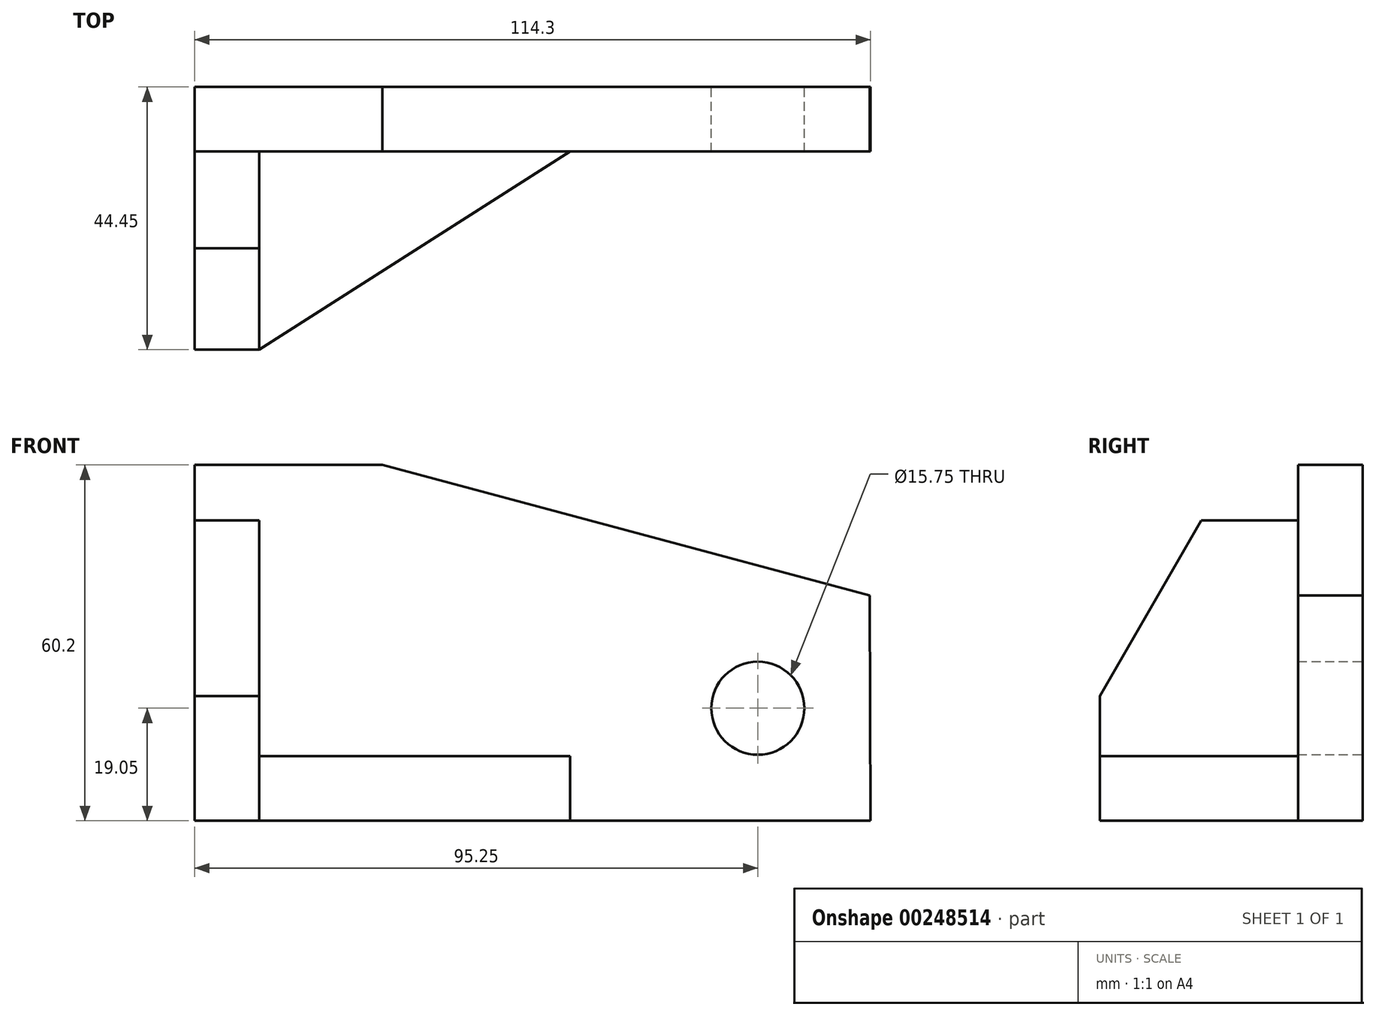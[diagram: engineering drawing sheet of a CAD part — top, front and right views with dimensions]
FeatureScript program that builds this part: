
annotation { "Feature Type Name" : "Feature", "Feature Type Description" : "" }
export const myFeature = defineFeature(function(context is Context, id is Id, definition is map)
    precondition{}
    {
        {
            var Q0;
            Q0=qCreatedBy(makeId("Top.planeOp"),FACE);
            var sketch = newSketch(context, id + "F0", { "sketchPlane" : qUnion([Q0])});
            skLineSegment(sketch, "E0", {"start": v(10.92, -10.92) * mm, "end": v(10.92, -44.45) * mm});
            skLineSegment(sketch, "E1", {"start": v(10.92, -10.92) * mm, "end": v(63.5, -10.92) * mm});
            skLineSegment(sketch, "E2", {"start": v(63.5, -10.92) * mm, "end": v(10.92, -44.45) * mm});
            skSolve(sketch);
        }
        {
            var Q0;
            Q0=qCreatedBy(makeId("Right.planeOp"),FACE);
            var sketch = newSketch(context, id + "F1", { "sketchPlane" : qUnion([Q0])});
            skLineSegment(sketch, "E3", {"start": v(0, 0) * mm, "end": v(-44.45, 0) * mm});
            skLineSegment(sketch, "E4", {"start": v(-44.45, 0) * mm, "end": v(-44.45, 21.08) * mm});
            skLineSegment(sketch, "E5", {"start": v(-44.45, 21.08) * mm, "end": v(-44.45, 50.8) * mm, "construction": true});
            skPoint(sketch, "E6", {"position": v(-10.92, 0) * mm});
            skPoint(sketch, "E7", {"position": v(0, 0) * mm});
            skLineSegment(sketch, "E8", {"start": v(-44.45, 50.8) * mm, "end": v(-27.3, 50.8) * mm, "construction": true});
            skLineSegment(sketch, "E9", {"start": v(-10.92, 50.8) * mm, "end": v(-27.3, 50.8) * mm});
            skLineSegment(sketch, "E10", {"start": v(-44.45, 21.08) * mm, "end": v(-27.3, 50.8) * mm});
            skLineSegment(sketch, "E11", {"start": v(-10.92, 0) * mm, "end": v(-10.92, 50.8) * mm});
            skSolve(sketch);
        }
        {
            var Q0;
            {var subQ0=sQuery(id+"F1.wireOp",EDGE,"E4");Q0=makeQuery(id+"F1.imprint","IMPRINT",FACE,{"disambiguationData":[TD([[makeQuery(id+"F1.imprint","IMPRINT",EDGE,{"derivedFrom":subQ0}),-1.0]])]});}
            extrude(context, id + "F2", {"entities" : qUnion([Q0]), "depth" : 10.92 * mm});
        }
        {
            var Q0;
            Q0=makeQuery(id+"F0.imprint","IMPRINT",FACE,{"disambiguationData":[TD([[makeQuery(id+"F0.imprint","IMPRINT",EDGE,{"derivedFrom":sQuery(id+"F0.wireOp",EDGE,"E0")}),1.0]])]});
            extrude(context, id + "F3", {"entities" : qUnion([Q0]), "operationType" : NewBodyOperationType.ADD, "depth" : 10.92 * mm});
        }
        {
            var Q0;
            Q0=qCreatedBy(makeId("Front.planeOp"),FACE);
            var sketch = newSketch(context, id + "F4", { "sketchPlane" : qUnion([Q0])});
            skLineSegment(sketch, "E12", {"start": v(0, 0) * mm, "end": v(114.3, 0) * mm});
            skLineSegment(sketch, "E13", {"start": v(0, 0) * mm, "end": v(0, 60.2) * mm});
            skLineSegment(sketch, "E14", {"start": v(0, 60.2) * mm, "end": v(31.75, 60.2) * mm});
            skPoint(sketch, "E15", {"position": v(114.19, 38.1) * mm});
            skLineSegment(sketch, "E16", {"start": v(31.75, 60.2) * mm, "end": v(114.19, 38.1) * mm});
            skLineSegment(sketch, "E17", {"start": v(31.75, 60.2) * mm, "end": v(114.3, 60.2) * mm, "construction": true});
            skLineSegment(sketch, "E18", {"start": v(114.19, 38.1) * mm, "end": v(114.3, 0) * mm});
            skLineSegment(sketch, "E19", {"start": v(114.3, 0) * mm, "end": v(95.25, 0) * mm});
            skPoint(sketch, "E20", {"position": v(95.25, 19.05) * mm});
            skCircle(sketch, "E21", {"center": v(95.25, 19.05) * mm, "radius": 7.87 * mm});
            skSolve(sketch);
        }
        {
            var Q0;
            Q0=makeQuery(id+"F4.imprint","IMPRINT",FACE,{"disambiguationData":[TD([[makeQuery(id+"F4.imprint","IMPRINT",EDGE,{"derivedFrom":sQuery(id+"F4.wireOp",EDGE,"E12")}),1.0]])]});
            extrude(context, id + "F5", {"entities" : qUnion([Q0]), "operationType" : NewBodyOperationType.ADD, "depth" : 10.92 * mm});
        }
    });
